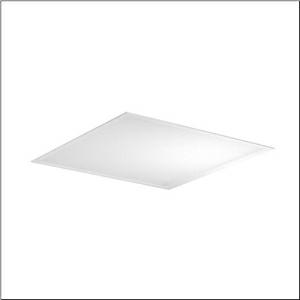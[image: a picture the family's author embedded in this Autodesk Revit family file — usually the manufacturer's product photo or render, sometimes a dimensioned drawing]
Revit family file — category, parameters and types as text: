
# Revit family: apollon_r__31_square_51mp12wd2442_6000
name_source: partatom
category: Lighting Fixtures
units: mm (PartAtom-declared; Revit-internal decimal feet)

## family parameters
Cut with Voids When Loaded = No
Host = Face
Light Source = No
Part Type = Normal
Room Calculation Point = No
Round Connector Dimension = Use Diameter
Shared = No

## types (1)
- Apollon® 31 square (1 x LED, 3800 lm, 27.5 W, 4000K)
    Apparent Load = 28 VA
    CIE Flux Codes = 61 87 97 100 100
    Color Rendering = 80
    Color Temperature = 4000K
    Default Elevation = 1800 mm
    Description = Apollon® 31 square, office luminaire, primary optical cover: micro prismatic cover, of PMMA, CAT 2 (L<= 3000cd/m²), light emission: direct distribution, primary light characteristic: symmetric, installation type: lay-in mounting, LED, rated luminous flux: 3.800lm, luminous efficacy: 138lm/W, light colour: 840, colour temperature: 4000K, control gear: DALI 2, Multilumen, with terminal, 5-pole, mains connection: 220..240V, AC/DC, 0/50..60Hz, rated input power: 28W, housing, of aluminium, traffic white (RAL 9016), module: M600, length: 595mm, width: 595mm, height: 62mm, recess depth: 180mm, housing upper side, of sheet steel, coated, protection rating (complete): IP20, protection rating (on room side): IP40, insulation class (complete): insulation class II (safety insulation), certification: CE, ENEC, impact resistance: IK03, permissible operating ambient temperature: -20..+40°C, permissible storage temperature: -20..+60°C, standard: EN 60598-2-22, packaging unit: 1 piece
    Height = 0 mm  [stored 0 ft]
    Lamp = 1 x LED
    Lamp Light Flux = 3800 lm
    Lamp Power = 27.5 W
    Lamp count = 1
    Length = 595 mm
    Luminous efficacy = 138 lm/W
    Manufacturer = Siteco
    ModVariant = No
    Model = 51MP12WD2442
    Mounting Place = Ceiling
    Mounting Type = Recessed
    Number of Poles = 1
    OnlyDefault = Yes
    Power Factor = 1
    Product Name = Apollon® 31 square
    Product group = office luminaire | ceiling recessed
    ProductGroupID = 401
    Protection Class = Protection class II
    Protection Degree = IP 20
    RLX_Detail_Level = 1
    RLX_Emergency_Light_Flux = 0 lm
    RLX_Emergency_Type = 0
    RLX_Emergency_Type_DB = No
    RlxData = <blob elided: 12573 chars, md5=07db65ff>
    Socket = socket
    Standby Power = 0 W
    System Light Flux = 3800 lm
    System Power = 28 W
    Type Comments = Product without accessories
    Type Image = l_1291035.jpg
    URL = http://relux.com
    VarID = ---
    Voltage = 0 V
    Weight = 0.00 kg
    Width = 595 mm

note: [stored X ft] marks values corroborated as IEEE doubles in the binary element streams (Revit-internal decimal feet)

## geometry (parser evidence)
native form markers: Sweep x9
no freeform markers — native parametric forms only
